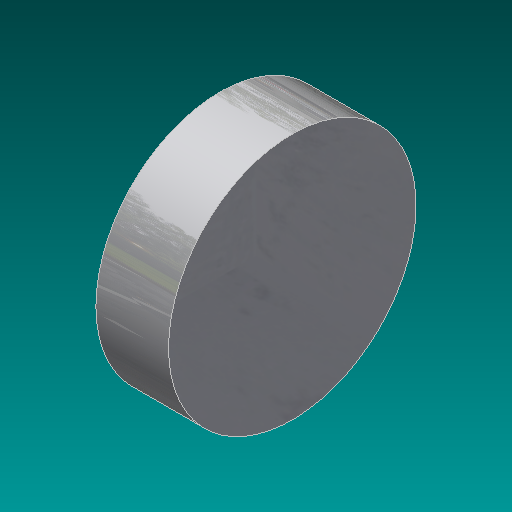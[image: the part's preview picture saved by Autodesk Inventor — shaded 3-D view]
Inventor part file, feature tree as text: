
AUTODESK INVENTOR PART (.ipt)
format: ipt  version: 2017 (Build 210142000, 142)  size: 204,800 bytes
history: native  units: mm (DEFAULTED — no unit token found)
features: other x4, revolve x1, sketch x1
ambient origin geometry x8: Origin, YZ Plane, XZ Plane, XY Plane, X Axis, Y Axis, Z Axis, Center Point
bodies: Solid1 (feature_tree)
feature tree (6):
  revolve  "Revolve1"  [1 undecoded]
  other  "Work Axis1"
  other  "Work Point1"
  other  "Work Point2"
  other  "Work Point3"
  sketch  "Sketch1"  dims[d4=90.0deg d0=48.641mm d1=5.5372mm d2=12.7mm d3=4.826mm]
note: 1 required parameter value undecoded (feature->parameter linkage not recoverable at this tier; creation-order binding heuristic only, values carry confidence <= 0.55)
